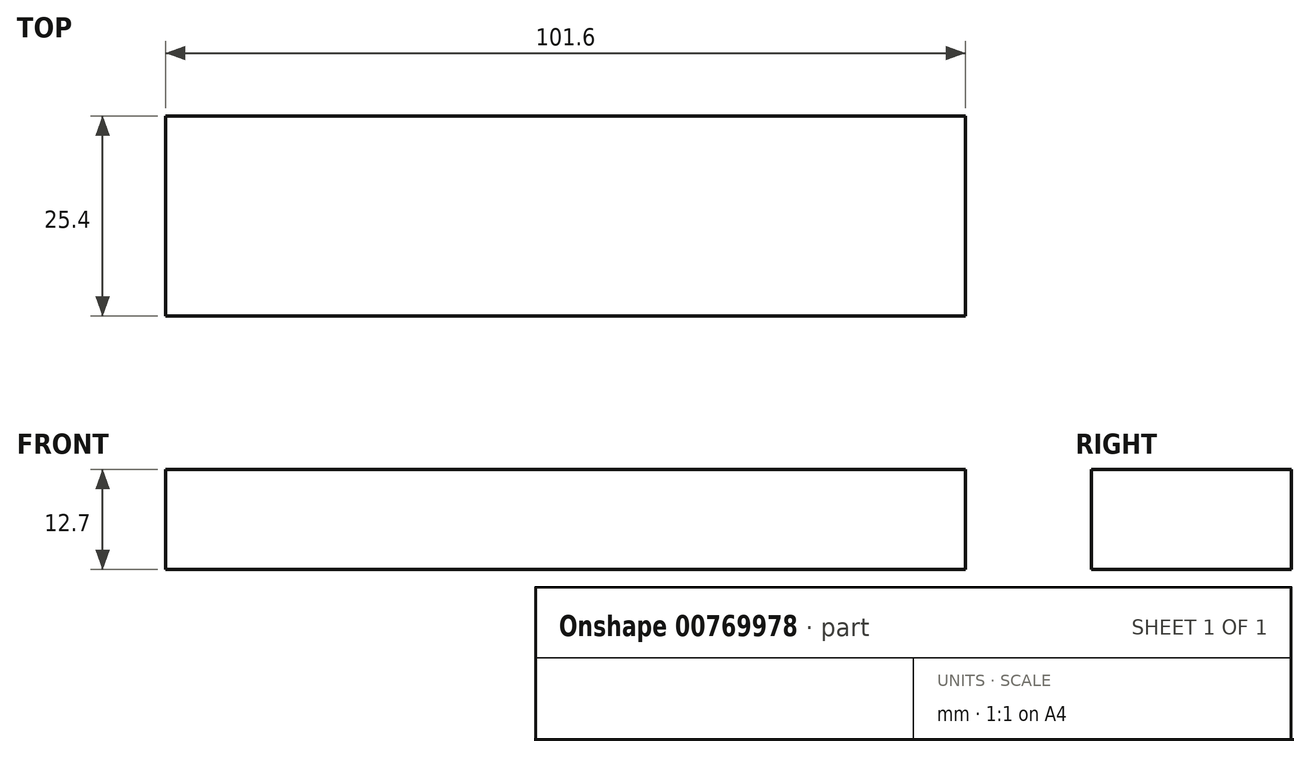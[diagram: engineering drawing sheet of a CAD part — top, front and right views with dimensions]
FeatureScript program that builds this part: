
annotation { "Feature Type Name" : "Feature", "Feature Type Description" : "" }
export const myFeature = defineFeature(function(context is Context, id is Id, definition is map)
    precondition{}
    {
        {
            var Q0;
            Q0=qCreatedBy(makeId("Front.planeOp"),FACE);
            var sketch = newSketch(context, id + "F0", { "sketchPlane" : qUnion([Q0])});
            skLineSegment(sketch, "E0.bottom", {"start": v(-57.13, 52.26) * mm, "end": v(44.47, 52.26) * mm});
            skLineSegment(sketch, "E0.top", {"start": v(-57.13, 39.56) * mm, "end": v(44.47, 39.56) * mm});
            skLineSegment(sketch, "E0.left", {"start": v(-57.13, 52.26) * mm, "end": v(-57.13, 39.56) * mm});
            skLineSegment(sketch, "E0.right", {"start": v(44.47, 52.26) * mm, "end": v(44.47, 39.56) * mm});
            skSolve(sketch);
        }
        {
            var Q0;
            Q0 = qSketchRegion(id + "F0", true);
            extrude(context, id + "F1", {"entities" : qUnion([Q0]), "depth" : 25.4 * mm, "offsetDistance" : 25.4 * mm});
        }
    });
